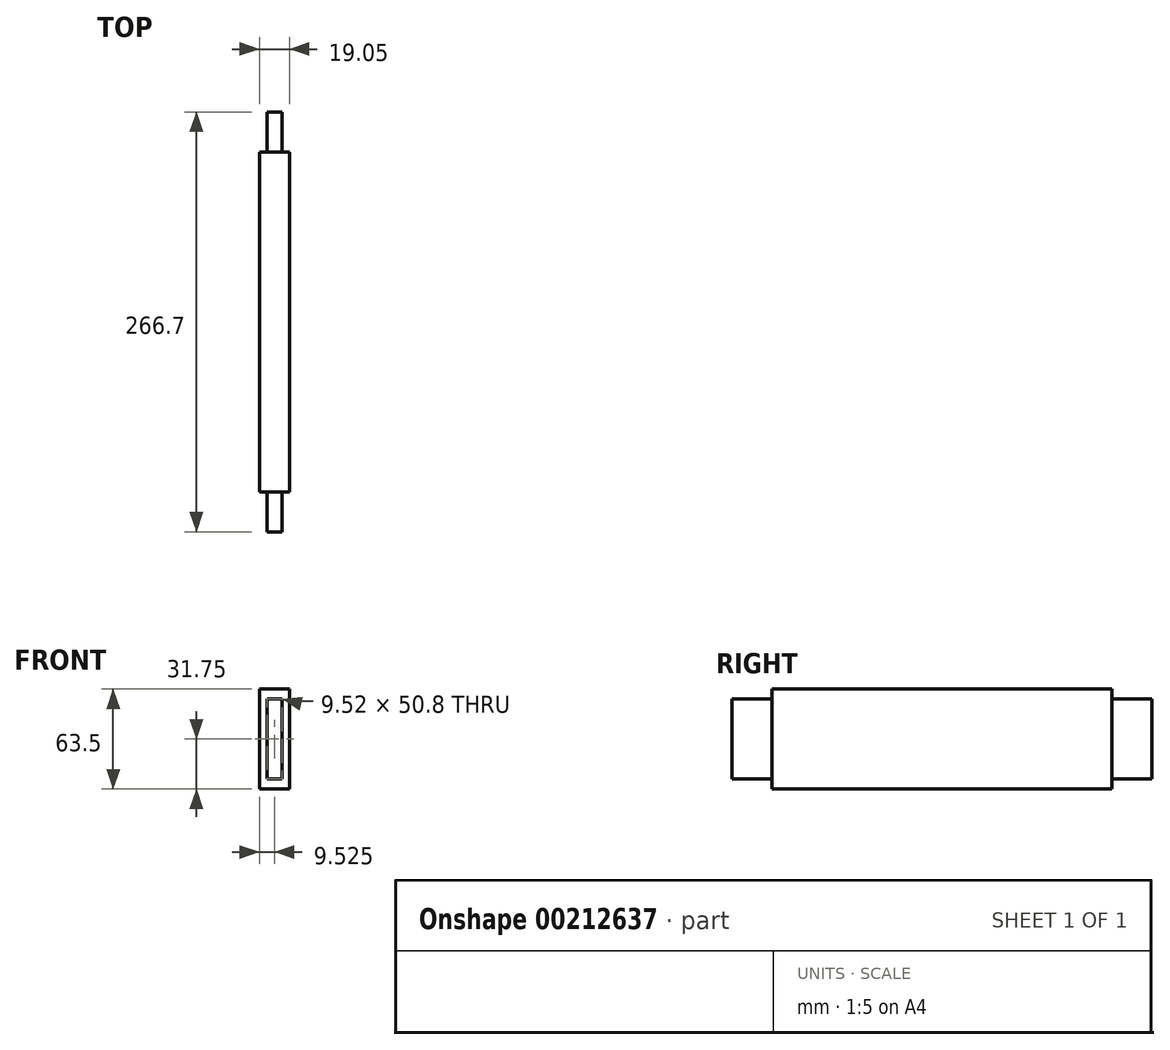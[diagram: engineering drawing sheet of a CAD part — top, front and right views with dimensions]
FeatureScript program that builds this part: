
annotation { "Feature Type Name" : "Feature", "Feature Type Description" : "" }
export const myFeature = defineFeature(function(context is Context, id is Id, definition is map)
    precondition{}
    {
        {
            var Q0;
            Q0=qCreatedBy(makeId("Right.planeOp"),FACE);
            var sketch = newSketch(context, id + "F0", { "sketchPlane" : qUnion([Q0])});
            skLineSegment(sketch, "E0.bottom", {"start": v(-107.95, 0) * mm, "end": v(107.95, 0) * mm});
            skLineSegment(sketch, "E0.top", {"start": v(-107.95, -63.5) * mm, "end": v(107.95, -63.5) * mm});
            skLineSegment(sketch, "E0.left", {"start": v(-107.95, 0) * mm, "end": v(-107.95, -63.5) * mm});
            skLineSegment(sketch, "E0.right", {"start": v(107.95, 0) * mm, "end": v(107.95, -63.5) * mm});
            skSolve(sketch);
        }
        {
            var Q0;
            Q0=makeQuery(id+"F0.imprint","IMPRINT",FACE,{"disambiguationData":[TD([[makeQuery(id+"F0.imprint","IMPRINT",EDGE,{"derivedFrom":sQuery(id+"F0.wireOp",EDGE,"E0.bottom")}),-1.0]])]});
            extrude(context, id + "F1", {"entities" : qUnion([Q0]), "depth" : 19.05 * mm});
        }
        {
            var Q0;
            Q0=makeQuery(id+"F1.opExtrude","SWEPT_FACE",FACE,{"disambiguationData":[OSD([sQuery(id+"F0.wireOp",EDGE,"E0.right")])]});
            var sketch = newSketch(context, id + "F2", { "sketchPlane" : qUnion([Q0])});
            skLineSegment(sketch, "E1.bottom", {"start": v(-14.29, -57.15) * mm, "end": v(-14.29, -6.35) * mm});
            skLineSegment(sketch, "E1.top", {"start": v(-4.76, -57.15) * mm, "end": v(-4.76, -6.35) * mm});
            skLineSegment(sketch, "E1.left", {"start": v(-14.29, -57.15) * mm, "end": v(-4.76, -57.15) * mm});
            skLineSegment(sketch, "E1.right", {"start": v(-14.29, -6.35) * mm, "end": v(-4.76, -6.35) * mm});
            skSolve(sketch);
        }
        {
            var Q0;
            Q0=makeQuery(id+"F2.imprint","IMPRINT",FACE,{"disambiguationData":[TD([[makeQuery(id+"F2.imprint","IMPRINT",EDGE,{"derivedFrom":sQuery(id+"F2.wireOp",EDGE,"E1.bottom")}),-1.0]])]});
            extrude(context, id + "F3", {"entities" : qUnion([Q0]), "operationType" : NewBodyOperationType.ADD, "depth" : 25.4 * mm});
        }
        {
            var Q0;
            Q0=makeQuery(id+"F1.opExtrude","SWEPT_FACE",FACE,{"disambiguationData":[OSD([sQuery(id+"F0.wireOp",EDGE,"E0.left")])]});
            var sketch = newSketch(context, id + "F4", { "sketchPlane" : qUnion([Q0])});
            skLineSegment(sketch, "E2.bottom", {"start": v(14.29, -6.35) * mm, "end": v(14.29, -57.15) * mm});
            skLineSegment(sketch, "E2.top", {"start": v(4.76, -6.35) * mm, "end": v(4.76, -57.15) * mm});
            skLineSegment(sketch, "E2.left", {"start": v(14.29, -6.35) * mm, "end": v(4.76, -6.35) * mm});
            skLineSegment(sketch, "E2.right", {"start": v(14.29, -57.15) * mm, "end": v(4.76, -57.15) * mm});
            skSolve(sketch);
        }
        {
            var Q0;
            Q0=makeQuery(id+"F4.imprint","IMPRINT",FACE,{"disambiguationData":[TD([[makeQuery(id+"F4.imprint","IMPRINT",EDGE,{"derivedFrom":sQuery(id+"F4.wireOp",EDGE,"E2.bottom")}),-1.0]])]});
            extrude(context, id + "F5", {"entities" : qUnion([Q0]), "operationType" : NewBodyOperationType.ADD, "depth" : 25.4 * mm});
        }
    });
